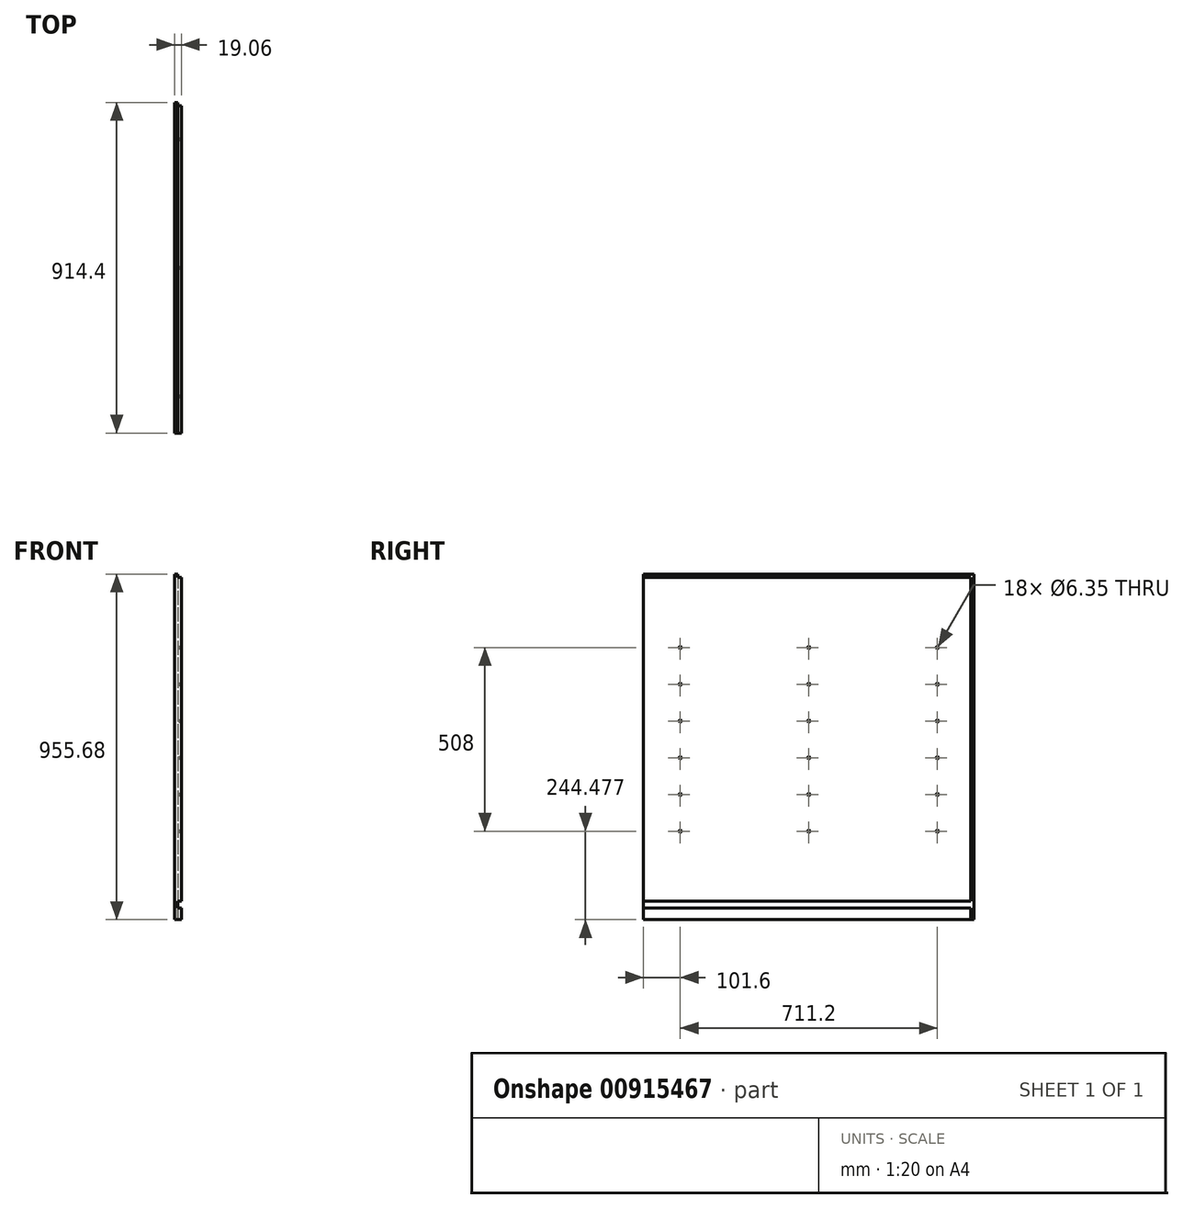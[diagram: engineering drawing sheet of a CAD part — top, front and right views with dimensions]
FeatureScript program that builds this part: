
annotation { "Feature Type Name" : "Feature", "Feature Type Description" : "" }
export const myFeature = defineFeature(function(context is Context, id is Id, definition is map)
    precondition{}
    {
        {
            var Q0;
            Q0=qCreatedBy(makeId("Right.planeOp"),FACE);
            var sketch = newSketch(context, id + "F0", { "sketchPlane" : qUnion([Q0])});
            skLineSegment(sketch, "E0.bottom", {"start": v(457.2, 477.84) * mm, "end": v(-457.2, 477.84) * mm});
            skLineSegment(sketch, "E0.top", {"start": v(457.2, -477.84) * mm, "end": v(-457.2, -477.84) * mm});
            skLineSegment(sketch, "E0.left", {"start": v(457.2, 477.84) * mm, "end": v(457.2, -477.84) * mm});
            skLineSegment(sketch, "E0.right", {"start": v(-457.2, 477.84) * mm, "end": v(-457.2, -477.84) * mm});
            skPoint(sketch, "E0.middle", {"position": v(0, 0) * mm});
            skSolve(sketch);
        }
        {
            var Q0;
            Q0=makeQuery(id+"F0.imprint","IMPRINT",FACE,{"disambiguationData":[TD([[makeQuery(id+"F0.imprint","IMPRINT",EDGE,{"derivedFrom":sQuery(id+"F0.wireOp",EDGE,"E0.bottom")}),1.0]])]});
            var sketch = newSketch(context, id + "F1", { "sketchPlane" : qUnion([Q0])});
            skLineSegment(sketch, "E1.bottom", {"start": v(-457.2, 468.31) * mm, "end": v(447.68, 468.31) * mm});
            skLineSegment(sketch, "E1.top", {"start": v(-457.2, -427.04) * mm, "end": v(447.68, -427.04) * mm});
            skLineSegment(sketch, "E1.left", {"start": v(-457.2, 468.31) * mm, "end": v(-457.2, -427.04) * mm});
            skLineSegment(sketch, "E1.right", {"start": v(447.68, 468.31) * mm, "end": v(447.68, -427.04) * mm});
            skLineSegment(sketch, "E2.bottom", {"start": v(-457.2, -477.84) * mm, "end": v(447.68, -477.84) * mm});
            skLineSegment(sketch, "E2.top", {"start": v(-457.2, -446.09) * mm, "end": v(447.68, -446.09) * mm});
            skLineSegment(sketch, "E2.left", {"start": v(-457.2, -477.84) * mm, "end": v(-457.2, -446.09) * mm});
            skLineSegment(sketch, "E2.right", {"start": v(447.68, -477.84) * mm, "end": v(447.68, -446.09) * mm});
            skSolve(sketch);
        }
        {
            var Q0;
            Q0=makeQuery(id+"F0.imprint","IMPRINT",FACE,{"disambiguationData":[TD([[makeQuery(id+"F0.imprint","IMPRINT",EDGE,{"derivedFrom":sQuery(id+"F0.wireOp",EDGE,"E0.bottom")}),1.0]])]});
            extrude(context, id + "F2", {"entities" : qUnion([Q0]), "oppositeDirection" : true, "depth" : 9.52 * mm, "offsetDistance" : 25.4 * mm});
        }
        {
            var Q0;
            Q0=qSketchRegion(id+"F1",true);
            extrude(context, id + "F3", {"entities" : qUnion([Q0]), "operationType" : NewBodyOperationType.ADD, "depth" : 9.52 * mm, "offsetDistance" : 25.4 * mm});
        }
        {
            var Q0;
            Q0=makeQuery(id+"F3.opExtrude","CAP_FACE",FACE,{"disambiguationData":[OSD([sQuery(id+"F1.wireOp",EDGE,"E1.bottom"),sQuery(id+"F1.wireOp",EDGE,"E1.top"),sQuery(id+"F1.wireOp",EDGE,"E1.left"),sQuery(id+"F1.wireOp",EDGE,"E1.right")])],"isStart":false});
            var sketch = newSketch(context, id + "F4", { "sketchPlane" : qUnion([Q0])});
            skPoint(sketch, "E3", {"position": v(-355.6, 274.64) * mm});
            skPoint(sketch, "E4.0.1.0", {"position": v(-355.6, 173.04) * mm});
            skPoint(sketch, "E4.0.2.0", {"position": v(-355.6, 71.44) * mm});
            skPoint(sketch, "E4.0.3.0", {"position": v(-355.6, -30.16) * mm});
            skPoint(sketch, "E4.0.4.0", {"position": v(-355.6, -131.76) * mm});
            skPoint(sketch, "E4.0.5.0", {"position": v(-355.6, -233.36) * mm});
            skPoint(sketch, "E4.1.0.0", {"position": v(0, 274.64) * mm});
            skPoint(sketch, "E4.1.1.0", {"position": v(0, 173.04) * mm});
            skPoint(sketch, "E4.1.2.0", {"position": v(0, 71.44) * mm});
            skPoint(sketch, "E4.1.3.0", {"position": v(0, -30.16) * mm});
            skPoint(sketch, "E4.1.4.0", {"position": v(0, -131.76) * mm});
            skPoint(sketch, "E4.1.5.0", {"position": v(0, -233.36) * mm});
            skPoint(sketch, "E4.2.0.0", {"position": v(355.6, 274.64) * mm});
            skPoint(sketch, "E4.2.1.0", {"position": v(355.6, 173.04) * mm});
            skPoint(sketch, "E4.2.2.0", {"position": v(355.6, 71.44) * mm});
            skPoint(sketch, "E4.2.3.0", {"position": v(355.6, -30.16) * mm});
            skPoint(sketch, "E4.2.4.0", {"position": v(355.6, -131.76) * mm});
            skPoint(sketch, "E4.2.5.0", {"position": v(355.6, -233.36) * mm});
            skLineSegment(sketch, "E4.direction1", {"start": v(-355.6, 274.64) * mm, "end": v(0, 274.64) * mm, "construction": true});
            skLineSegment(sketch, "E4.direction2", {"start": v(-355.6, 274.64) * mm, "end": v(-355.6, 173.04) * mm, "construction": true});
            skSolve(sketch);
        }
        {
            var Q0;
            Q0=sQuery(id+"F4.wireOp",VERTEX,"E3");
            var Q1;
            Q1=sQuery(id+"F4.wireOp",VERTEX,"E4.1.3.0");
            var Q2;
            Q2=sQuery(id+"F4.wireOp",VERTEX,"E4.0.1.0");
            var Q3;
            Q3=sQuery(id+"F4.wireOp",VERTEX,"E4.1.1.0");
            var Q4;
            Q4=sQuery(id+"F4.wireOp",VERTEX,"E4.2.1.0");
            var Q5;
            Q5=sQuery(id+"F4.wireOp",VERTEX,"E4.0.2.0");
            var Q6;
            Q6=sQuery(id+"F4.wireOp",VERTEX,"E4.2.3.0");
            var Q7;
            Q7=sQuery(id+"F4.wireOp",VERTEX,"E4.1.0.0");
            var Q8;
            Q8=sQuery(id+"F4.wireOp",VERTEX,"E4.1.4.0");
            var Q9;
            Q9=sQuery(id+"F4.wireOp",VERTEX,"E4.1.2.0");
            var Q10;
            Q10=sQuery(id+"F4.wireOp",VERTEX,"E4.0.4.0");
            var Q11;
            Q11=sQuery(id+"F4.wireOp",VERTEX,"E4.2.0.0");
            var Q12;
            Q12=sQuery(id+"F4.wireOp",VERTEX,"E4.2.5.0");
            var Q13;
            Q13=sQuery(id+"F4.wireOp",VERTEX,"E4.0.5.0");
            var Q14;
            Q14=sQuery(id+"F4.wireOp",VERTEX,"E4.2.4.0");
            var Q15;
            Q15=sQuery(id+"F4.wireOp",VERTEX,"E4.1.5.0");
            var Q16;
            Q16=sQuery(id+"F4.wireOp",VERTEX,"E4.0.3.0");
            var Q17;
            Q17=sQuery(id+"F4.wireOp",VERTEX,"E4.2.2.0");
            var Q18;
            Q18=makeQuery(id+"F2.opExtrude","SWEPT_BODY",BODY,{"disambiguationData":[OSD([sQuery(id+"F0.wireOp",EDGE,"E0.bottom"),sQuery(id+"F0.wireOp",EDGE,"E0.top"),sQuery(id+"F0.wireOp",EDGE,"E0.left"),sQuery(id+"F0.wireOp",EDGE,"E0.right")])]});
            hole(context, id + "F5", {"style" : HoleStyle.SIMPLE, "endStyle" : HoleEndStyle.BLIND, "holeDiameter" : 6.35 * mm, "majorDiameter" : 6.35 * mm, "holeDepth" : 6.35 * mm, "isTappedThrough" : true, "tappedDepth" : 12.7 * mm, "tapClearance" : 3, "startFromSketch" : true, "locations" : qUnion([Q0, Q1, Q2, Q3, Q4, Q5, Q6, Q7, Q8, Q9, Q10, Q11, Q12, Q13, Q14, Q15, Q16, Q17]), "scope" : qUnion([Q18])});
        }
    });
